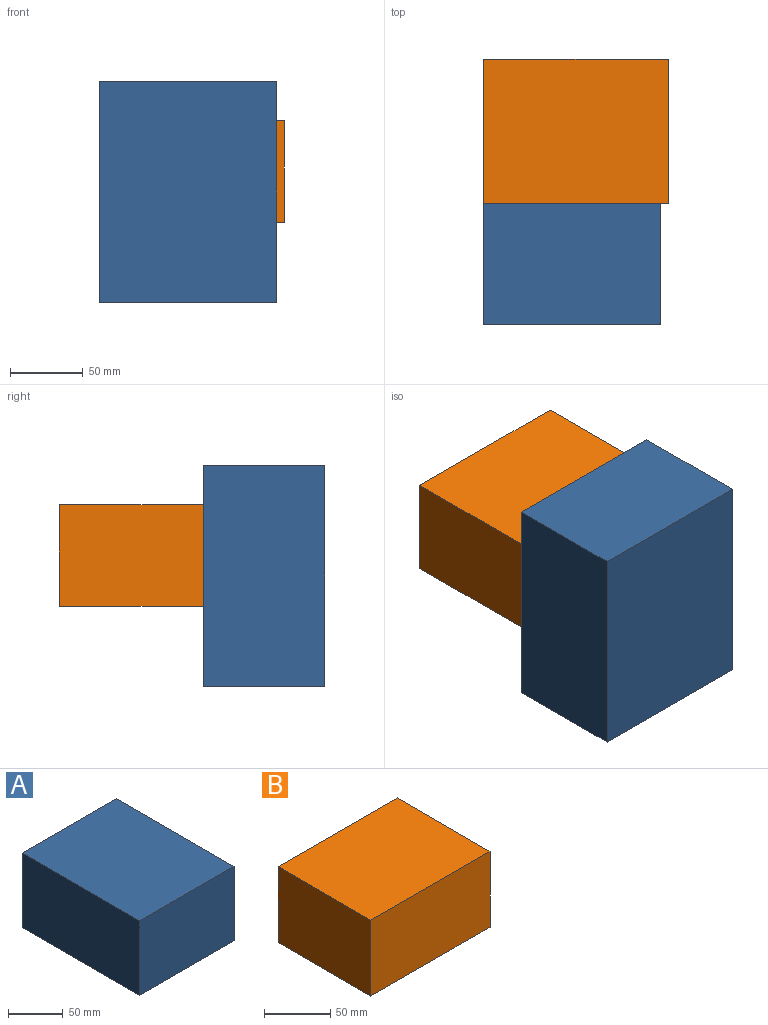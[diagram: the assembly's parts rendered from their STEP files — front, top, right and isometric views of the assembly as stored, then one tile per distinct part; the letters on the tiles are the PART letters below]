
ASSEMBLY  parts=2 mates=2
PART A: 6 faces, bbox 121.9x152x83.3 mm
  f0: plane 152x121.88mm, normal (0,0,-1), area 18525.8mm2, adj f1,f3,f4,f5
  f1: plane 152x83.32mm, normal (1,0,0), area 12665mm2, adj f0,f2,f4,f5
  f2: plane 152x121.88mm, normal (0,0,1), area 18525.8mm2, adj f1,f3,f4,f5
  f3: plane 152x83.32mm, normal (-1,0,0), area 12665mm2, adj f0,f2,f4,f5
  f4: plane 121.88x83.32mm, normal (0,-1,0), area 10155.4mm2, adj f0,f1,f2,f3
  f5: plane 121.88x83.32mm, normal (0,1,0), area 10155.4mm2, adj f0,f1,f2,f3
PART B: 6 faces, bbox 126.9x99x70 mm
  f0: plane 99x69.96mm, normal (1,0,0), area 6926.2mm2, adj f1,f3,f4,f5
  f1: plane 126.94x99mm, normal (0,0,1), area 12567.2mm2, adj f0,f2,f4,f5
  f2: plane 99x69.96mm, normal (-1,0,0), area 6926.2mm2, adj f1,f3,f4,f5
  f3: plane 126.94x99mm, normal (0,0,-1), area 12567.2mm2, adj f0,f2,f4,f5
  f4: plane 126.94x69.96mm, normal (0,-1,0), area 8881mm2, adj f0,f1,f2,f3
  f5: plane 126.94x69.96mm, normal (0,1,0), area 8881mm2, adj f0,f1,f2,f3
PLACE A rot(axis=(1,0,0),90deg) t=(60.94,-41.66,152)mm
PLACE B t=(63.47,99,90.08)mm
MATE planar A.f0 <-> B.f4  axis (0,1,0) through (60.94,0,76)mm
MATE planar B.f2 <-> A.f3  axis (-1,0,0) through (0,49.5,90.08)mm
